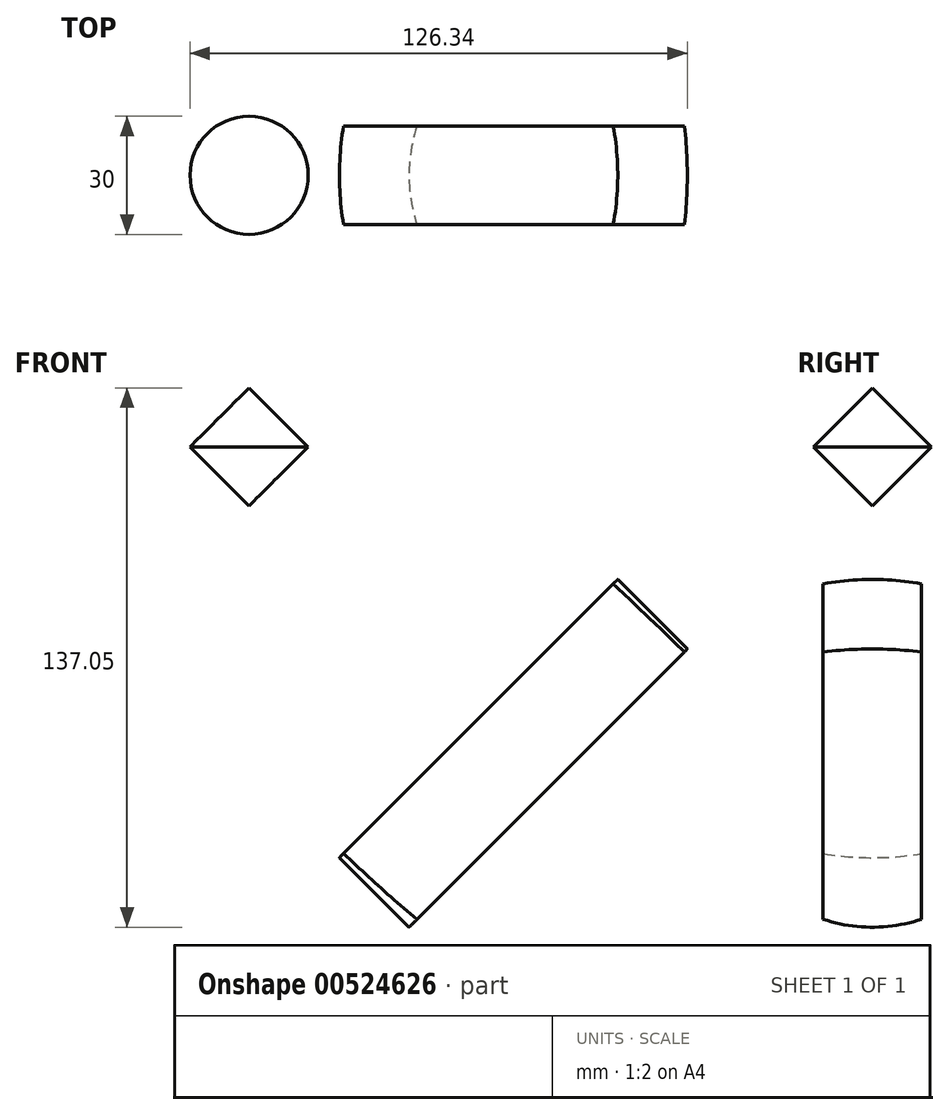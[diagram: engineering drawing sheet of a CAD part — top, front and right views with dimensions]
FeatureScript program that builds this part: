
annotation { "Feature Type Name" : "Feature", "Feature Type Description" : "" }
export const myFeature = defineFeature(function(context is Context, id is Id, definition is map)
    precondition{}
    {
        {
            var Q0;
            Q0=qCreatedBy(makeId("Front.planeOp"),FACE);
            var sketch = newSketch(context, id + "F0", { "sketchPlane" : qUnion([Q0])});
            skLineSegment(sketch, "E0", {"start": v(0, 80.4) * mm, "end": v(0, -82.74) * mm, "construction": true});
            skLineSegment(sketch, "E1", {"start": v(0, 70.71) * mm, "end": v(-70.71, 0) * mm});
            skLineSegment(sketch, "E2", {"start": v(-70.71, 0) * mm, "end": v(0, -70.71) * mm});
            skLineSegment(sketch, "E3", {"start": v(0, -70.71) * mm, "end": v(0, 70.71) * mm});
            skSolve(sketch);
        }
        {
            var Q0;
            Q0=qSketchRegion(id+"F0",true);
            var Q1;
            Q1=sQuery(id+"F0.wireOp",EDGE,"E0");
            revolve(context, id + "F1", {"entities" : qUnion([Q0]), "axis" : qUnion([Q1]), "revolveType" : RevolveType.FULL});
        }
        {
            var Q0;
            Q0=qCreatedBy(makeId("Front.planeOp"),FACE);
            var sketch = newSketch(context, id + "F2", { "sketchPlane" : qUnion([Q0])});
            skLineSegment(sketch, "E4", {"start": v(-45, 70.71) * mm, "end": v(-60, 55.71) * mm});
            skLineSegment(sketch, "E5", {"start": v(-60, 55.71) * mm, "end": v(-60, 85.71) * mm});
            skLineSegment(sketch, "E6", {"start": v(-60, 85.71) * mm, "end": v(-45, 70.71) * mm});
            skLineSegment(sketch, "E7", {"start": v(-60, 47.19) * mm, "end": v(-60, 91.17) * mm, "construction": true});
            skSolve(sketch);
        }
        {
            var Q0;
            Q0=makeQuery(id+"F2.imprint","IMPRINT",FACE,{"disambiguationData":[TD([[makeQuery(id+"F2.imprint","IMPRINT",EDGE,{"derivedFrom":sQuery(id+"F2.wireOp",EDGE,"E4")}),-1.0]])]});
            var Q1;
            Q1=sQuery(id+"F2.wireOp",EDGE,"E7");
            revolve(context, id + "F3", {"entities" : qUnion([Q0]), "axis" : qUnion([Q1]), "revolveType" : RevolveType.FULL});
        }
        {
            var Q0;
            Q0=qCreatedBy(makeId("Front.planeOp"),FACE);
            var sketch = newSketch(context, id + "F4", { "sketchPlane" : qUnion([Q0])});
            skLineSegment(sketch, "E8", {"start": v(50, 53.39) * mm, "end": v(-56.07, -52.68) * mm});
            skLineSegment(sketch, "E9", {"start": v(-56.07, -52.68) * mm, "end": v(-38.39, -70.36) * mm});
            skLineSegment(sketch, "E10", {"start": v(-38.39, -70.36) * mm, "end": v(67.68, 35.71) * mm});
            skLineSegment(sketch, "E11", {"start": v(67.68, 35.71) * mm, "end": v(50, 53.39) * mm});
            skLineSegment(sketch, "E12", {"start": v(-55.42, -15.3) * mm, "end": v(-70.71, 0) * mm});
            skSolve(sketch);
        }
        {
            var Q0;
            Q0=qSketchRegion(id+"F4",true);
            extrude(context, id + "F5", {"entities" : qUnion([Q0]), "endBound" : BoundingType.SYMMETRIC, "depth" : 25 * mm, "offsetDistance" : 25 * mm});
        }
        {
            var Q0;
            Q0=makeQuery(id+"F5.opExtrude","SWEPT_BODY",BODY,{"disambiguationData":[OSD([sQuery(id+"F4.wireOp",EDGE,"E8"),sQuery(id+"F4.wireOp",EDGE,"E9"),sQuery(id+"F4.wireOp",EDGE,"E10"),sQuery(id+"F4.wireOp",EDGE,"E11")])]});
            var Q1;
            Q1=makeQuery(id+"F1.opRevolve","SWEPT_BODY",BODY,{"disambiguationData":[OSD([sQuery(id+"F0.wireOp",EDGE,"E1"),sQuery(id+"F0.wireOp",EDGE,"E2"),sQuery(id+"F0.wireOp",EDGE,"E3")])]});
            booleanBodies(context, id + "F6", {"operationType" : BooleanOperationType.INTERSECTION, "tools" : qUnion([Q0, Q1])});
        }
    });
